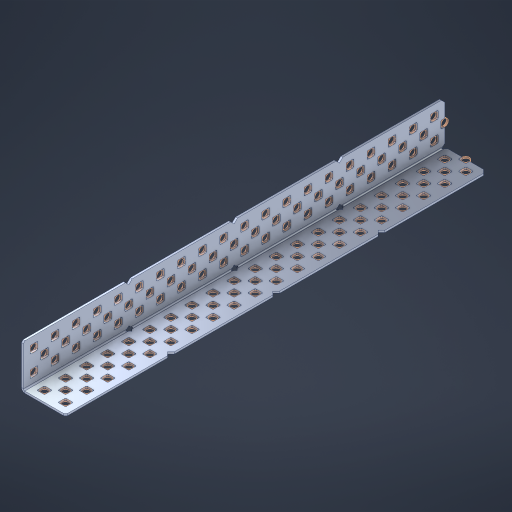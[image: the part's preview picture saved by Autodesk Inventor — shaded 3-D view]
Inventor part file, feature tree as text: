
AUTODESK INVENTOR PART (.ipt)
format: ipt  version: 2023 (Build 270158000, 158)  size: 1,494,016 bytes
history: native  units: in
note: dims shown in document units (in); Inventor stores cm internally (conversion verified against a paired STEP export)
features: other x126, extrude x118, sheet_metal_op x8, sketch x7, pattern_linear x2, mirror x1, chamfer x1
ambient origin geometry x8: Origin, YZ Plane, XZ Plane, XY Plane, X Axis, Y Axis, Z Axis, Center Point
bodies: Solid1 (feature_tree), Body (feature_tree)
feature tree (263):
  sheet_metal_op  "Flanges"
  sheet_metal_op  "Body Pattern"
  pattern_linear  "Center Pattern"  Spacing1=1.0in  [1 undecoded]
  other  "Arc Length"
  pattern_linear  "Notch Pattern"  Spacing1=0.1875in  [1 undecoded]
  other  "Diagonal Plane"
  mirror  "Everything Mirrored"
  chamfer  "End Chamfer"
  sketch  "Sketch1"  dims[d0=1.0in]
  other  "Plate1"
  sketch  "Sketch2"  dims[d1=10.0in]
  other  "Plate2"
  sheet_metal_op  "Bend1"
  sheet_metal_op  "Corner1"
  sketch  "Sketch8"  dims[d2=0.0469in]
  sketch  "Sketch9"  dims[d3=0.0469in]
  other  "Srf91"
  sheet_metal_op  "Body Pattern Sketch"
  other  "Srf92"
  sketch  "Sketch13"  dims[d4=0.0234in]
  sketch  "Sketch15"  dims[d5=0.0938in]
  sketch  "Sketch16"  dims[d6=0.0469in d7=1.0in d8=90.0deg d9=0.0312in d10=0.1875in d11=0.0469in d12=0.0469in d49=0.182in d50=0.02in d52=0.25in d53=0.0469in d54=0.0in d55=0.172in d56=1.0in d57=0.0in d60=7.874in d62=0.5in d63=0.7874in d65=0.5in d85=0.1473in d86=0.1659in d89=0.0469in d90=0.0in d91=0.04in d92=0.0491in d95=2.5in d96=0.04in d97=0.25in d98=45.0deg d99=0.25in d106=0.182in d107=0.02in d108=0.5in d110=0.0469in d111=0.0in d112=0.172in d113=0.5in d114=0.0in d117=0.5in d123=0.25in d125=0.25in d126=0.0491in d127=0.1227in d128=0.08in d129=0.04in d130=2.5in]
  other  "Srf786"
  other  "Srf856"
  other  "Srf857"
  other  "Srf858"
  other  "Srf859"
  other  "Srf860"
  other  "Srf861"
  other  "Srf889"
  other  "Srf890"
  other  "Srf891"
  other  "Srf1275"
  other  "Srf1276"
  other  "Srf1278"
  other  "Srf1279"
  other  "Srf1280"
  other  "Srf1281"
  other  "Srf1282"
  other  "Srf1283"
  other  "Srf1277"
  other  "Srf1285"
  other  "Srf1286"
  other  "Srf1287"
  other  "Srf1383"
  other  "Srf1384"
  other  "Srf1385"
  other  "Srf1386"
  other  "Srf1387"
  other  "Srf1388"
  other  "Srf1389"
  other  "Srf1390"
  other  "Srf1391"
  other  "Srf1392"
  other  "Srf1393"
  other  "Srf1394"
  other  "Srf1395"
  other  "Srf1396"
  other  "Srf1397"
  other  "Srf1398"
  other  "Srf1399"
  other  "Srf1400"
  other  "Srf1401"
  other  "Srf1402"
  other  "Srf1403"
  other  "Srf1404"
  other  "Srf1405"
  other  "Srf1406"
  other  "Srf1407"
  other  "Srf1408"
  other  "Srf1409"
  other  "Srf1410"
  other  "Srf1411"
  other  "Srf1412"
  other  "Srf1413"
  other  "Srf1414"
  other  "Srf1445"
  other  "Srf1446"
  other  "Srf1447"
  other  "Srf1448"
  other  "Srf1449"
  other  "Srf1450"
  other  "Srf1451"
  other  "Srf1452"
  other  "Srf1453"
  other  "Srf1454"
  other  "Srf1455"
  other  "Srf1456"
  other  "Srf1457"
  other  "Srf1458"
  other  "Srf1459"
  other  "Srf1460"
  other  "Srf1475"
  other  "Srf1476"
  other  "Srf1477"
  other  "Srf1478"
  other  "Srf1479"
  other  "Srf1480"
  other  "Srf1481"
  other  "Srf1482"
  other  "Srf1483"
  other  "Srf1484"
  other  "Srf1485"
  other  "Srf1486"
  other  "Srf1487"
  other  "Srf1488"
  other  "Srf1489"
  other  "Srf1490"
  other  "Srf1491"
  other  "Srf1492"
  other  "Srf1493"
  other  "Srf1494"
  other  "Srf1495"
  other  "Srf1496"
  other  "Srf1497"
  other  "Srf1498"
  other  "Srf1499"
  other  "Srf1500"
  other  "Srf1501"
  other  "Srf1502"
  other  "Srf1503"
  other  "Srf1504"
  other  "Srf1505"
  other  "Srf1506"
  other  "Srf1537"
  other  "Srf1538"
  other  "Srf1539"
  other  "Srf1540"
  other  "Srf1541"
  other  "Srf1542"
  other  "Srf1543"
  other  "Srf1544"
  other  "Srf1545"
  other  "Srf1546"
  other  "Srf1547"
  other  "Srf1548"
  other  "Srf1549"
  other  "Srf1550"
  other  "Srf1551"
  other  "Srf1552"
  sheet_metal_op  "Body Stamp"
  sheet_metal_op  "Body Circle"
  other  "Center Stamp"
  other  "Center Circle"
  sheet_metal_op  "Notch"
  extrude  "ExtrusionSrf92"  Depth=0.0469in
  extrude  "ExtrusionSrf856"  Depth=0.0469in
  extrude  "ExtrusionSrf857"  Depth=2.5in
  extrude  "ExtrusionSrf858"  Depth=0.02in
  extrude  "ExtrusionSrf859"  Depth=2.5in
  extrude  "ExtrusionSrf860"  Depth=0.0469in
  extrude  "ExtrusionSrf861"  TaperAngle=0.0deg  [1 undecoded]
  extrude  "ExtrusionSrf889"  Depth=2.5in
  extrude  "ExtrusionSrf890"  Depth=1.0in TaperAngle=0.0deg
  extrude  "ExtrusionSrf891"  Depth=2.5in
  extrude  "ExtrusionSrf1275"  Depth=0.5in
  extrude  "ExtrusionSrf1276"  Depth=2.5in
  extrude  "ExtrusionSrf1277"  Depth=2.5in
  extrude  "ExtrusionSrf1278"  Depth=0.0469in
  extrude  "ExtrusionSrf1279"  Depth=2.5in TaperAngle=0.0deg
  extrude  "ExtrusionSrf1280"  Depth=2.5in
  extrude  "ExtrusionSrf1281"  Depth=2.5in TaperAngle=45.0deg
  extrude  "ExtrusionSrf1282"  Depth=2.5in
  extrude  "ExtrusionSrf1345"  Depth=2.5in
  extrude  "ExtrusionSrf1346"  Depth=0.02in
  extrude  "ExtrusionSrf1347"  Depth=0.5in
  extrude  "ExtrusionSrf1348"  Depth=0.0469in
  extrude  "ExtrusionSrf1383"  TaperAngle=0.0deg  [1 undecoded]
  extrude  "ExtrusionSrf1384"  Depth=2.5in
  extrude  "ExtrusionSrf1385"  Depth=0.5in TaperAngle=0.0deg
  extrude  "ExtrusionSrf1386"  Depth=0.5in
  extrude  "ExtrusionSrf1387"  Depth=2.5in
  extrude  "ExtrusionSrf1388"  Depth=2.5in
  extrude  "ExtrusionSrf1389"  Depth=2.5in
  extrude  "ExtrusionSrf1390"  Depth=2.5in
  extrude  "ExtrusionSrf1391"  Depth=2.5in
  extrude  "ExtrusionSrf1392"  Depth=2.5in
  extrude  "ExtrusionSrf1393"  Depth=2.5in
  extrude  "ExtrusionSrf1394"  [1 undecoded]
  extrude  "ExtrusionSrf1395"  [1 undecoded]
  extrude  "ExtrusionSrf1396"  [1 undecoded]
  extrude  "ExtrusionSrf1397"  [1 undecoded]
  extrude  "ExtrusionSrf1398"  [1 undecoded]
  extrude  "ExtrusionSrf1399"  [1 undecoded]
  extrude  "ExtrusionSrf1400"  [1 undecoded]
  extrude  "ExtrusionSrf1401"  [1 undecoded]
  extrude  "ExtrusionSrf1402"  [1 undecoded]
  extrude  "ExtrusionSrf1403"  [1 undecoded]
  extrude  "ExtrusionSrf1404"  [1 undecoded]
  extrude  "ExtrusionSrf1405"  [1 undecoded]
  extrude  "ExtrusionSrf1406"  [1 undecoded]
  extrude  "ExtrusionSrf1407"  [1 undecoded]
  extrude  "ExtrusionSrf1408"  [1 undecoded]
  extrude  "ExtrusionSrf1409"  [1 undecoded]
  extrude  "ExtrusionSrf1410"  [1 undecoded]
  extrude  "ExtrusionSrf1411"  [1 undecoded]
  extrude  "ExtrusionSrf1412"  [1 undecoded]
  extrude  "ExtrusionSrf1413"  [1 undecoded]
  extrude  "ExtrusionSrf1414"  [1 undecoded]
  extrude  "ExtrusionSrf1445"  [1 undecoded]
  extrude  "ExtrusionSrf1446"  [1 undecoded]
  extrude  "ExtrusionSrf1447"  [1 undecoded]
  extrude  "ExtrusionSrf1448"  [1 undecoded]
  extrude  "ExtrusionSrf1449"  [1 undecoded]
  extrude  "ExtrusionSrf1450"  [1 undecoded]
  extrude  "ExtrusionSrf1451"  [1 undecoded]
  extrude  "ExtrusionSrf1452"  [1 undecoded]
  extrude  "ExtrusionSrf1453"  [1 undecoded]
  extrude  "ExtrusionSrf1454"  [1 undecoded]
  extrude  "ExtrusionSrf1455"  [1 undecoded]
  extrude  "ExtrusionSrf1456"  [1 undecoded]
  extrude  "ExtrusionSrf1457"  [1 undecoded]
  extrude  "ExtrusionSrf1458"  [1 undecoded]
  extrude  "ExtrusionSrf1459"  [1 undecoded]
  extrude  "ExtrusionSrf1460"  [1 undecoded]
  extrude  "ExtrusionSrf1475"  [1 undecoded]
  extrude  "ExtrusionSrf1476"  [1 undecoded]
  extrude  "ExtrusionSrf1477"  [1 undecoded]
  extrude  "ExtrusionSrf1478"  [1 undecoded]
  extrude  "ExtrusionSrf1479"  [1 undecoded]
  extrude  "ExtrusionSrf1480"  [1 undecoded]
  extrude  "ExtrusionSrf1481"  [1 undecoded]
  extrude  "ExtrusionSrf1482"  [1 undecoded]
  extrude  "ExtrusionSrf1483"  [1 undecoded]
  extrude  "ExtrusionSrf1484"  [1 undecoded]
  extrude  "ExtrusionSrf1485"  [1 undecoded]
  extrude  "ExtrusionSrf1486"  [1 undecoded]
  extrude  "ExtrusionSrf1487"  [1 undecoded]
  extrude  "ExtrusionSrf1488"  [1 undecoded]
  extrude  "ExtrusionSrf1489"  [1 undecoded]
  extrude  "ExtrusionSrf1490"  [1 undecoded]
  extrude  "ExtrusionSrf1491"  [1 undecoded]
  extrude  "ExtrusionSrf1492"  [1 undecoded]
  extrude  "ExtrusionSrf1493"  [1 undecoded]
  extrude  "ExtrusionSrf1494"  [1 undecoded]
  extrude  "ExtrusionSrf1495"  [1 undecoded]
  extrude  "ExtrusionSrf1496"  [1 undecoded]
  extrude  "ExtrusionSrf1497"  [1 undecoded]
  extrude  "ExtrusionSrf1498"  [1 undecoded]
  extrude  "ExtrusionSrf1499"  [1 undecoded]
  extrude  "ExtrusionSrf1500"  [1 undecoded]
  extrude  "ExtrusionSrf1501"  [1 undecoded]
  extrude  "ExtrusionSrf1502"  [1 undecoded]
  extrude  "ExtrusionSrf1503"  [1 undecoded]
  extrude  "ExtrusionSrf1504"  [1 undecoded]
  extrude  "ExtrusionSrf1505"  [1 undecoded]
  extrude  "ExtrusionSrf1506"  [1 undecoded]
  extrude  "ExtrusionSrf1537"  [1 undecoded]
  extrude  "ExtrusionSrf1538"  [1 undecoded]
  extrude  "ExtrusionSrf1539"  [1 undecoded]
  extrude  "ExtrusionSrf1540"  [1 undecoded]
  extrude  "ExtrusionSrf1541"  [1 undecoded]
  extrude  "ExtrusionSrf1542"  [1 undecoded]
  extrude  "ExtrusionSrf1543"  [1 undecoded]
  extrude  "ExtrusionSrf1544"  [1 undecoded]
  extrude  "ExtrusionSrf1545"  [1 undecoded]
  extrude  "ExtrusionSrf1546"  [1 undecoded]
  extrude  "ExtrusionSrf1547"  [1 undecoded]
  extrude  "ExtrusionSrf1548"  [1 undecoded]
  extrude  "ExtrusionSrf1549"  [1 undecoded]
  extrude  "ExtrusionSrf1550"  [1 undecoded]
  extrude  "ExtrusionSrf1551"  [1 undecoded]
  extrude  "ExtrusionSrf1552"  [1 undecoded]
note: 89 required parameter values undecoded (feature->parameter linkage not recoverable at this tier; creation-order binding heuristic only, values carry confidence <= 0.55)
